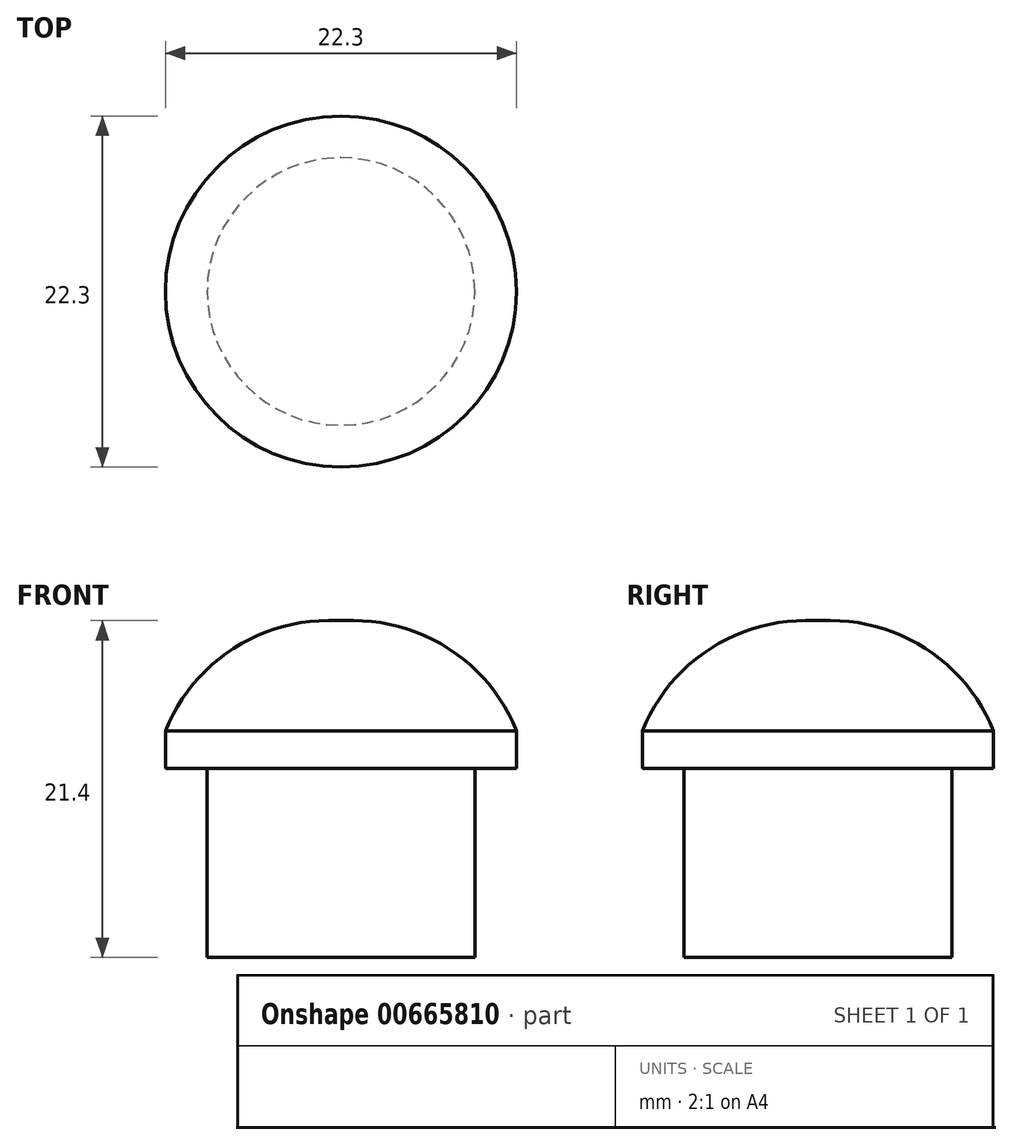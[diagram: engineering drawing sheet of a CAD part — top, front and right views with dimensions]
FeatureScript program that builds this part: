
annotation { "Feature Type Name" : "Feature", "Feature Type Description" : "" }
export const myFeature = defineFeature(function(context is Context, id is Id, definition is map)
    precondition{}
    {
        {
            var Q0;
            Q0=qCreatedBy(makeId("Top.planeOp"),FACE);
            var sketch = newSketch(context, id + "F0", { "sketchPlane" : qUnion([Q0])});
            skCircle(sketch, "E0", {"center": v(0, 0) * mm, "radius": 8.5 * mm});
            skSolve(sketch);
        }
        {
            var Q0;
            Q0 = qSketchRegion(id + "F0", true);
            extrude(context, id + "F1", {"entities" : qUnion([Q0]), "depth" : 12 * mm, "offsetDistance" : 25 * mm});
        }
        {
            var Q0;
            Q0=makeQuery(id+"F1.opExtrude","CAP_FACE",FACE,{"disambiguationData":[OSD([sQuery(id+"F0.wireOp",EDGE,"E0")])],"isStart":false});
            var sketch = newSketch(context, id + "F2", { "sketchPlane" : qUnion([Q0])});
            skCircle(sketch, "E1", {"center": v(0, 0) * mm, "radius": 11.15 * mm});
            skSolve(sketch);
        }
        {
            var Q0;
            Q0 = qSketchRegion(id + "F2", true);
            extrude(context, id + "F3", {"entities" : qUnion([Q0]), "operationType" : NewBodyOperationType.ADD, "depth" : 2.4 * mm, "offsetDistance" : 25 * mm});
        }
        {
            var Q0;
            Q0=makeQuery(id+"F3.opExtrude","CAP_FACE",FACE,{"disambiguationData":[OSD([sQuery(id+"F2.wireOp",EDGE,"E1")])],"isStart":false});
            var sketch = newSketch(context, id + "F4", { "sketchPlane" : qUnion([Q0])});
            skCircle(sketch, "E2", {"center": v(0, 0) * mm, "radius": 11.15 * mm});
            skSolve(sketch);
        }
        {
            var Q0;
            Q0=makeQuery(id+"F4.imprint","IMPRINT",FACE,{"disambiguationData":[TD([[makeQuery(id+"F4.imprint","IMPRINT",EDGE,{"derivedFrom":sQuery(id+"F4.wireOp",EDGE,"E2")}),1.0]])]});
            var Q1;
            Q1=sQuery(id+"F4.wireOp",EDGE,"E2");
            extrude(context, id + "F5", {"entities" : qUnion([Q0]), "surfaceEntities" : qUnion([Q1]), "depth" : 7 * mm, "offsetDistance" : 25 * mm});
        }
        {
            var Q0;
            Q0=makeQuery(id+"F5.opExtrude","CAP_EDGE",EDGE,{"disambiguationData":[OSD([sQuery(id+"F4.wireOp",EDGE,"E2")])],"isStart":false});
            fillet(context, id + "F6", {"entities" : qUnion([Q0]), "radius" : 11.15 * mm, "tangentPropagation" : true, "allowEdgeOverflow" : false});
        }
    });
